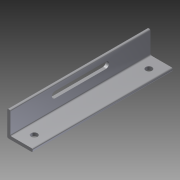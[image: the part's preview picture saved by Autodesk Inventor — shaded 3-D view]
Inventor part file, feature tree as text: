
AUTODESK INVENTOR PART (.ipt)
format: ipt  version: 2012 (Build 160160000, 160)  size: 118,272 bytes
history: native  units: in
note: dims shown in document units (in); Inventor stores cm internally (conversion verified against a paired STEP export)
features: extrude x3, sketch x3, fillet x2
ambient origin geometry x8: Origin, YZ Plane, XZ Plane, XY Plane, X Axis, Y Axis, Z Axis, Center Point
bodies: Solid1 (feature_tree)
feature tree (8):
  extrude  "Extrusion1"  Depth=0.125in
  fillet  "Fillet1"  Radius=0.125in
  fillet  "Fillet2"  Radius=1.0in
  extrude  "Extrusion2"  Depth=0.05in
  extrude  "Extrusion3"  Depth=0.25in
  sketch  "Sketch1"  dims[d1=1.0in d2=0.125in d3=0.125in d4=1.0in]
  sketch  "Sketch2"  dims[d5=5.5in d6=0.0in d7=0.05in]
  sketch  "Sketch3"  dims[d8=0.05in d9=0.25in d10=0.25in d11=0.5in d12=0.5in d13=6.0in d14=0.0in d18=6.0in d19=0.0in d20=1.75in d21=2.0in d22=5.5in]
